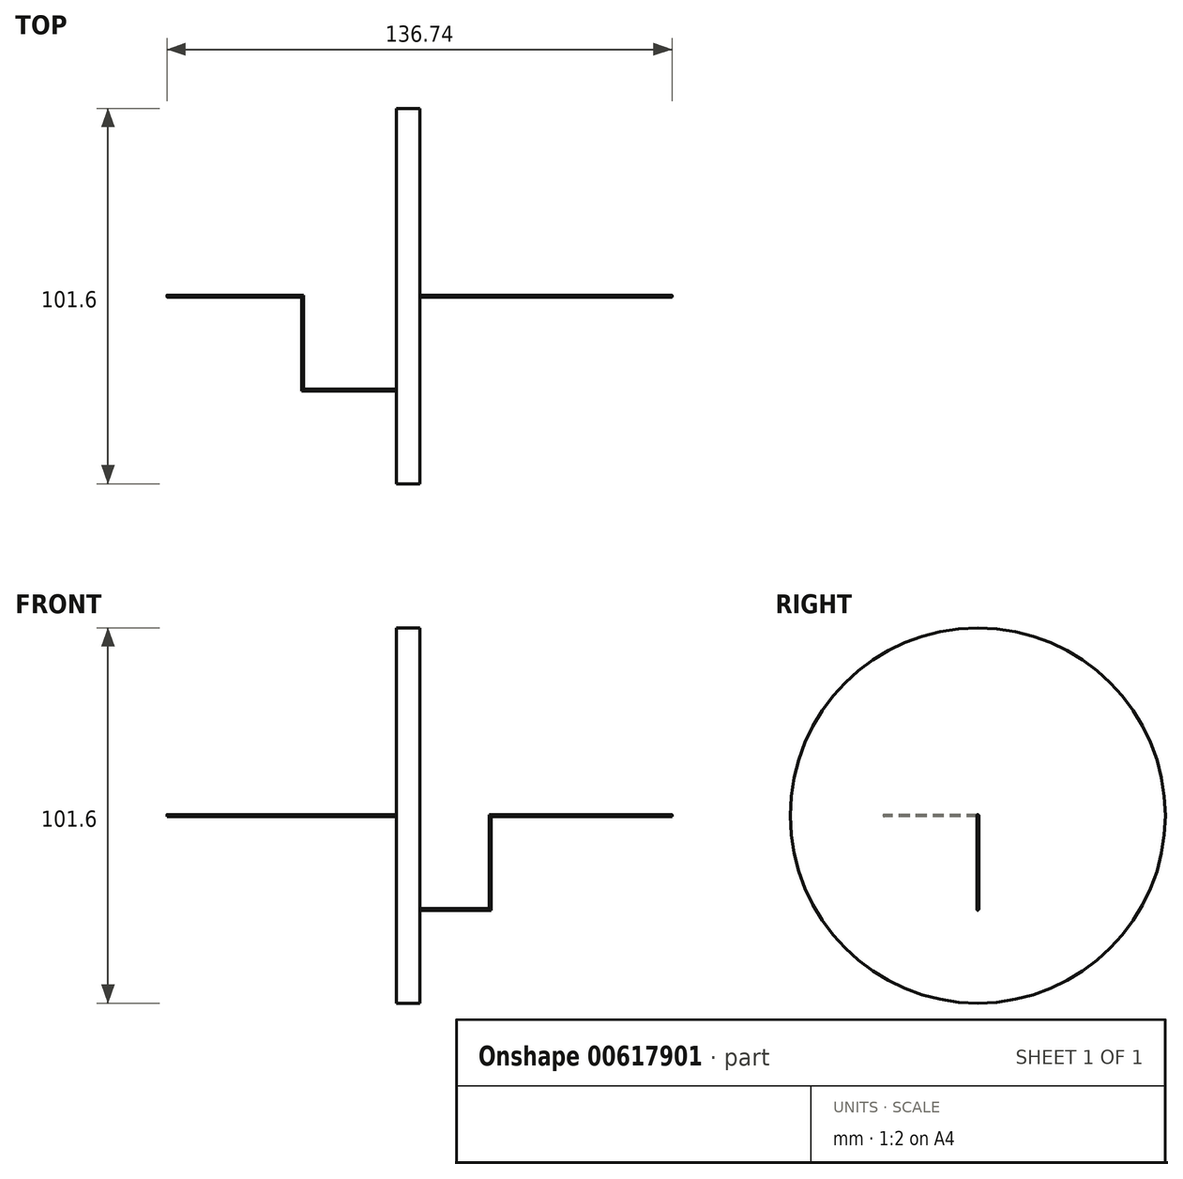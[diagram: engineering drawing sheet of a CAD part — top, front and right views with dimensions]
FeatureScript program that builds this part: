
annotation { "Feature Type Name" : "Feature", "Feature Type Description" : "" }
export const myFeature = defineFeature(function(context is Context, id is Id, definition is map)
    precondition{}
    {
        {
            var Q0;
            Q0=qCreatedBy(makeId("Front.planeOp"),FACE);
            var sketch = newSketch(context, id + "F0", { "sketchPlane" : qUnion([Q0])});
            skLineSegment(sketch, "E0.bottom", {"start": v(0, 0) * mm, "end": v(6.35, 0) * mm});
            skLineSegment(sketch, "E0.top", {"start": v(0, 50.8) * mm, "end": v(6.35, 50.8) * mm});
            skLineSegment(sketch, "E0.left", {"start": v(0, 0) * mm, "end": v(0, 50.8) * mm});
            skLineSegment(sketch, "E0.right", {"start": v(6.35, 0) * mm, "end": v(6.35, 50.8) * mm});
            skSolve(sketch);
        }
        {
            var Q0;
            Q0=makeQuery(id+"F0.imprint","IMPRINT",FACE,{"disambiguationData":[TD([[makeQuery(id+"F0.imprint","IMPRINT",EDGE,{"derivedFrom":sQuery(id+"F0.wireOp",EDGE,"E0.bottom")}),1.0]])]});
            var Q1;
            Q1=sQuery(id+"F0.wireOp",EDGE,"E0.bottom");
            revolve(context, id + "F1", {"entities" : qUnion([Q0]), "axis" : qUnion([Q1]), "revolveType" : RevolveType.FULL});
        }
        {
            var Q0;
            Q0=qCreatedBy(makeId("Top.planeOp"),FACE);
            var sketch = newSketch(context, id + "F2", { "sketchPlane" : qUnion([Q0])});
            skLineSegment(sketch, "E1", {"start": v(0, 0) * mm, "end": v(0, -25.4) * mm});
            skLineSegment(sketch, "E2", {"start": v(0, -25.4) * mm, "end": v(-25.4, -25.4) * mm});
            skLineSegment(sketch, "E3", {"start": v(-25.4, -25.4) * mm, "end": v(-25.4, 0) * mm});
            skLineSegment(sketch, "E4", {"start": v(-25.4, 0) * mm, "end": v(-62.07, 0) * mm});
            skSolve(sketch);
        }
        {
            var Q0;
            Q0=qCreatedBy(makeId("Right.planeOp"),FACE);
            cPlane(context, id + "F3", {"entities" : qUnion([Q0]), "cplaneType" : CPlaneType.OFFSET, "offset" : 33.02 * mm, "oppositeDirection" : true, "width" : 152.4 * mm, "height" : 152.4 * mm});
        }
        {
            var Q0;
            Q0=qCreatedBy(id+"F3.planeOp",FACE);
            var sketch = newSketch(context, id + "F4", { "sketchPlane" : qUnion([Q0])});
            skCircle(sketch, "E5", {"center": v(0, 0) * mm, "radius": 0.25 * mm});
            skSolve(sketch);
        }
        {
            var Q0;
            Q0 = qSketchRegion(id + "F4", true);
            var Q1;
            Q1=sQuery(id+"F2.wireOp",EDGE,"E3");
            var Q2;
            Q2=sQuery(id+"F2.wireOp",EDGE,"E2");
            var Q3;
            Q3=sQuery(id+"F2.wireOp",EDGE,"E4");
            sweep(context, id + "F5", {"operationType" : NewBodyOperationType.ADD, "profiles" : qUnion([Q0]), "path" : qUnion([Q1, Q2, Q3])});
        }
        {
            var Q0;
            Q0=qCreatedBy(makeId("Front.planeOp"),FACE);
            var sketch = newSketch(context, id + "F6", { "sketchPlane" : qUnion([Q0])});
            skLineSegment(sketch, "E6", {"start": v(0, 0) * mm, "end": v(0, -25.4) * mm});
            skLineSegment(sketch, "E7", {"start": v(0, -25.4) * mm, "end": v(25.4, -25.4) * mm});
            skLineSegment(sketch, "E8", {"start": v(25.4, -25.4) * mm, "end": v(25.4, 0) * mm});
            skLineSegment(sketch, "E9", {"start": v(25.4, 0) * mm, "end": v(74.67, 0) * mm});
            skSolve(sketch);
        }
        {
            var Q0;
            Q0=qCreatedBy(makeId("Right.planeOp"),FACE);
            cPlane(context, id + "F7", {"entities" : qUnion([Q0]), "cplaneType" : CPlaneType.OFFSET, "offset" : 33.02 * mm, "width" : 152.4 * mm, "height" : 152.4 * mm});
        }
        {
            var Q0;
            Q0=qCreatedBy(id+"F7.planeOp",FACE);
            var sketch = newSketch(context, id + "F8", { "sketchPlane" : qUnion([Q0])});
            skCircle(sketch, "E10", {"center": v(0, 0) * mm, "radius": 0.25 * mm});
            skSolve(sketch);
        }
        {
            var Q0;
            Q0 = qSketchRegion(id + "F8", true);
            var Q1;
            Q1=sQuery(id+"F6.wireOp",EDGE,"E9");
            var Q2;
            Q2=sQuery(id+"F6.wireOp",EDGE,"E8");
            var Q3;
            Q3=sQuery(id+"F6.wireOp",EDGE,"E7");
            sweep(context, id + "F9", {"operationType" : NewBodyOperationType.ADD, "profiles" : qUnion([Q0]), "path" : qUnion([Q1, Q2, Q3])});
        }
    });
